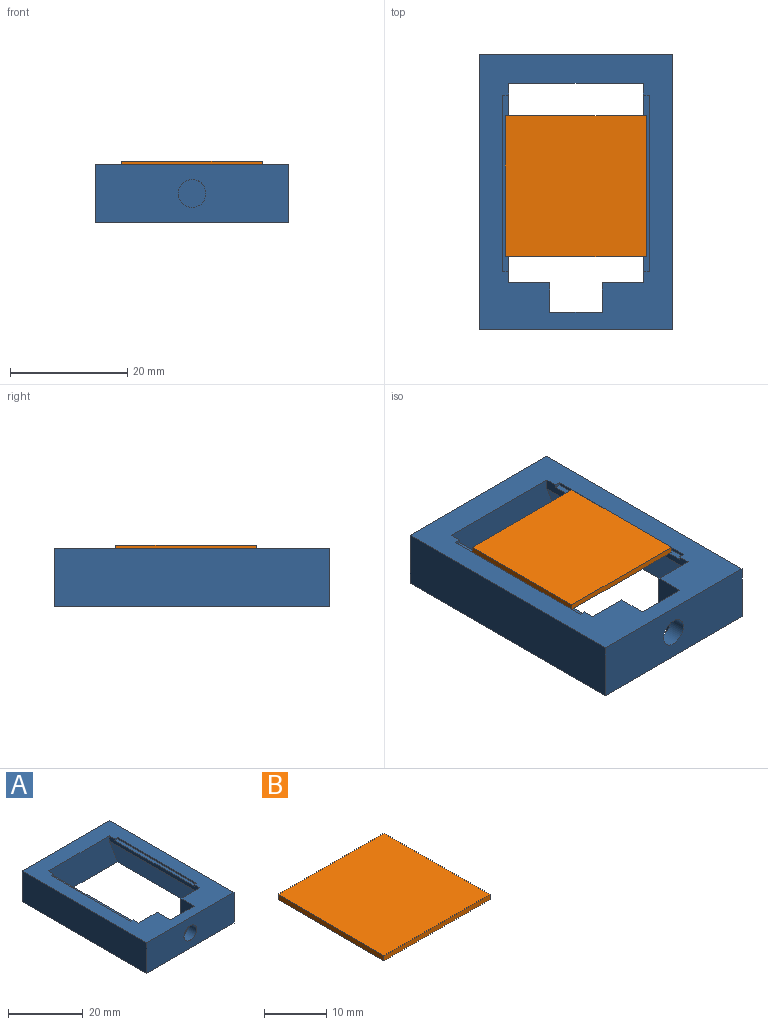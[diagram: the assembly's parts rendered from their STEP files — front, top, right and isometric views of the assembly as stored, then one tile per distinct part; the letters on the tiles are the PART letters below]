
ASSEMBLY  parts=2 mates=1
PART A: 25 faces, bbox 33x47x10 mm
  f0: plane 34x1.76mm, normal (-1,0,0), area 44.8mm2, adj f1,f5,f11,f18,f20,f21,f23
  f1: plane 47x33mm, normal (0,0,1), area 664mm2, adj f0,f2,f3,f4,f5,f6,f7,f8
  f2: plane 33x10mm, normal (0,1,0), area 330mm2, adj f1,f3,f12,f13
  f3: plane 47x10mm, normal (-1,0,0), area 470mm2, adj f1,f2,f4,f13
  f4: plane 33x10mm, normal (0,-1,0), area 312.3mm2, adj f1,f3,f12,f13,f22
  f5: plane 10x10mm, normal (0,1,0), area 82.4mm2, adj f0,f1,f6,f13,f23
  f6: plane 10x5mm, normal (-1,0,0), area 50mm2, adj f1,f5,f7,f13
  f7: plane 10x9mm, normal (0,1,0), area 72.3mm2, adj f1,f6,f8,f13,f22
  f8: plane 10x5mm, normal (1,0,0), area 50mm2, adj f1,f7,f9,f13
  f9: plane 10x10mm, normal (0,1,0), area 82.4mm2, adj f1,f8,f10,f13,f24
  f10: plane 34x1.76mm, normal (1,0,0), area 44.8mm2, adj f1,f9,f11,f14,f15,f17,f24
  f11: plane 29x10mm, normal (0,-1,0), area 254.7mm2, adj f0,f1,f10,f13,f23,f24
  f12: plane 47x10mm, normal (1,0,0), area 470mm2, adj f1,f2,f4,f13
  f13: plane 47x33mm, normal (0,0,-1), area 520mm2, adj f2,f3,f4,f5,f6,f7,f8,f9
  f14: plane 1x0.5mm, normal (0,1,0), area 0.5mm2, adj f1,f10,f16,f17
  f15: plane 1x0.5mm, normal (0,-1,0), area 0.5mm2, adj f1,f10,f16,f17
  f16: plane 30x0.5mm, normal (1,0,0), area 15mm2, adj f1,f14,f15,f17
  f17: plane 30x1mm, normal (0,0,1), area 30mm2, adj f10,f14,f15,f16
  f18: plane 1x0.5mm, normal (0,1,0), area 0.5mm2, adj f0,f1,f19,f21
  f19: plane 30x0.5mm, normal (-1,0,0), area 15mm2, adj f1,f18,f20,f21
  f20: plane 1x0.5mm, normal (0,-1,0), area 0.5mm2, adj f0,f1,f19,f21
  f21: plane 30x1mm, normal (0,0,1), area 30mm2, adj f0,f18,f19,f20
  f22: cylinder r=2.38mm len=4.75mm, axis (0,-1,0), area 44.8mm2, adj f4,f7
  f23: plane 34x8.24mm, normal (-0.94,0,-0.34), area 298.2mm2, adj f0,f5,f11,f13
  f24: plane 34x8.24mm, normal (0.94,0,-0.34), area 298.2mm2, adj f9,f10,f11,f13
PART B: 6 faces, bbox 24x24x1 mm
  f0: plane 24x1mm, normal (0,-1,0), area 24mm2, adj f1,f3,f4,f5
  f1: plane 24x1mm, normal (1,0,0), area 24mm2, adj f0,f2,f4,f5
  f2: plane 24x1mm, normal (0,1,0), area 24mm2, adj f1,f3,f4,f5
  f3: plane 24x1mm, normal (-1,0,0), area 24mm2, adj f0,f2,f4,f5
  f4: plane 24x24mm, normal (0,0,1), area 576mm2, adj f0,f1,f2,f3
  f5: plane 24x24mm, normal (0,0,-1), area 576mm2, adj f0,f1,f2,f3
PLACE A t=(0.97,3.36,-3.05)mm fixed
PLACE B t=(0.94,2.85,6.45)mm
MATE planar B.f5 <-> A.f17  axis (0,0,-1) through (-11.06,2.85,6.45)mm
